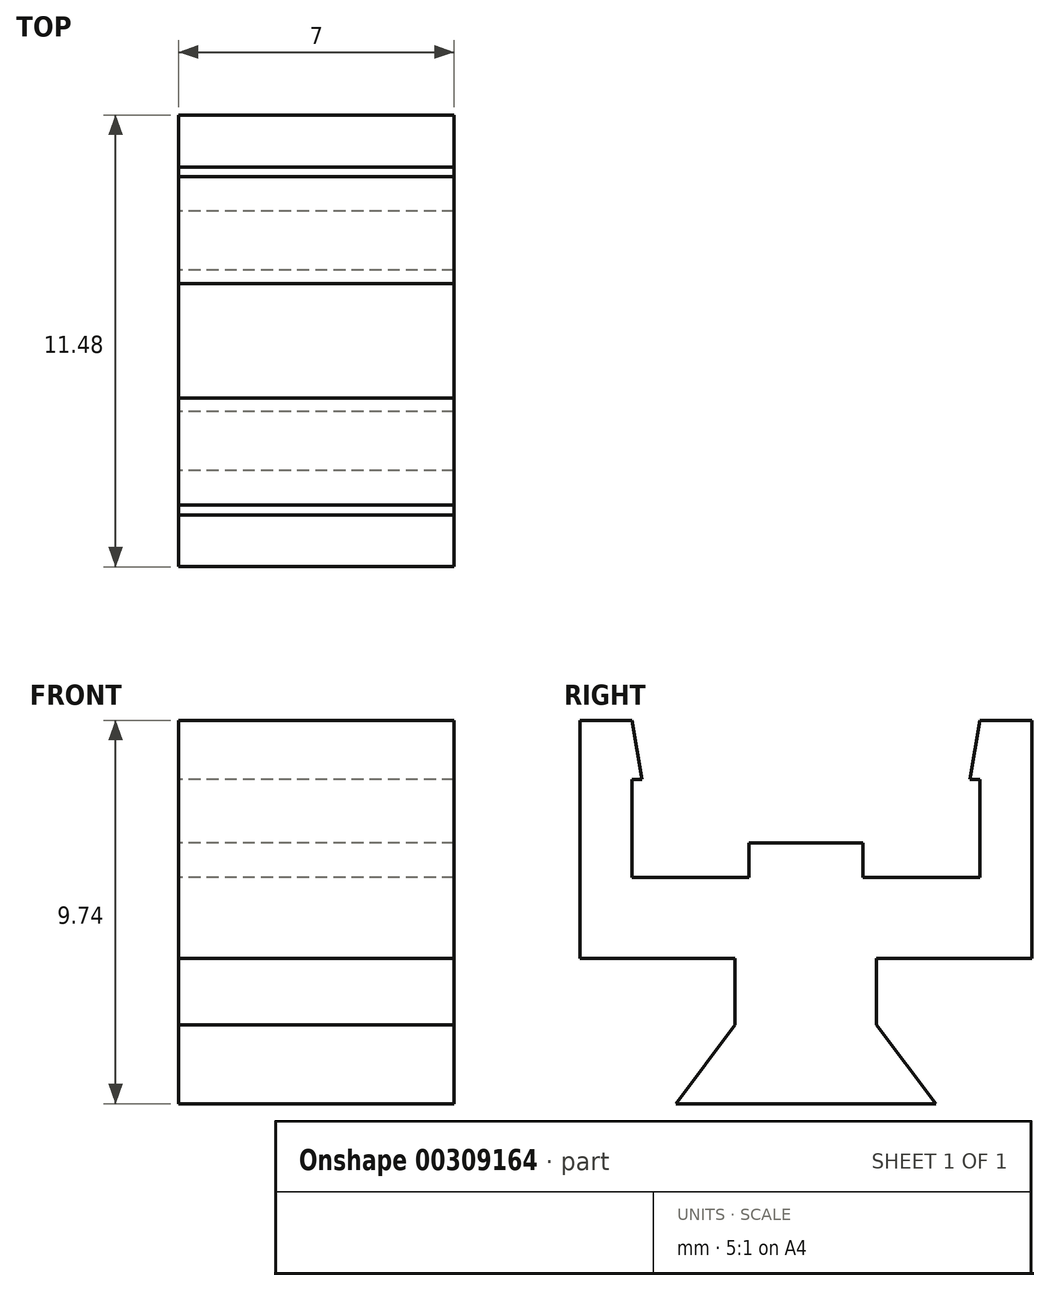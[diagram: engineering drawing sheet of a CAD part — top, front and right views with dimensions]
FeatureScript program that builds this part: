
annotation { "Feature Type Name" : "Feature", "Feature Type Description" : "" }
export const myFeature = defineFeature(function(context is Context, id is Id, definition is map)
    precondition{}
    {
        {
            var Q0;
            Q0=qCreatedBy(makeId("Right.planeOp"),FACE);
            var sketch = newSketch(context, id + "F0", { "sketchPlane" : qUnion([Q0])});
            skLineSegment(sketch, "E0", {"start": v(-2.14, -4.23) * mm, "end": v(1.46, -4.23) * mm, "construction": true});
            skLineSegment(sketch, "E1", {"start": v(-2.14, -4.23) * mm, "end": v(-3.34, -4.23) * mm, "construction": true});
            skLineSegment(sketch, "E2", {"start": v(1.46, -4.23) * mm, "end": v(2.66, -4.23) * mm, "construction": true});
            skLineSegment(sketch, "E3", {"start": v(-2.14, -4.23) * mm, "end": v(-2.14, -2.54) * mm});
            skLineSegment(sketch, "E4.MirrorCS", {"start": v(1.46, -4.23) * mm, "end": v(1.46, -2.54) * mm});
            skLineSegment(sketch, "E5", {"start": v(-2.14, -2.54) * mm, "end": v(1.46, -2.54) * mm});
            skLineSegment(sketch, "E6", {"start": v(-2.14, -4.23) * mm, "end": v(1.46, -4.23) * mm});
            skLineSegment(sketch, "E7.bottom", {"start": v(1.46, -2.54) * mm, "end": v(2.66, -2.54) * mm});
            skLineSegment(sketch, "E8.MirrorCS", {"start": v(-2.14, -2.54) * mm, "end": v(-3.34, -2.54) * mm});
            skLineSegment(sketch, "E9", {"start": v(-3.34, -2.54) * mm, "end": v(-3.34, -0.49) * mm});
            skLineSegment(sketch, "E10", {"start": v(-3.34, -0.49) * mm, "end": v(-0.34, -0.49) * mm});
            skLineSegment(sketch, "E11.MirrorCS", {"start": v(2.66, -0.49) * mm, "end": v(-0.34, -0.49) * mm});
            skLineSegment(sketch, "E12.MirrorCS", {"start": v(2.66, -2.54) * mm, "end": v(2.66, -0.49) * mm});
            skLineSegment(sketch, "E13", {"start": v(-1.8, -0.49) * mm, "end": v(-1.8, 0.4) * mm});
            skLineSegment(sketch, "E14", {"start": v(-1.8, 0.4) * mm, "end": v(-0.34, 0.4) * mm});
            skLineSegment(sketch, "E15.MirrorCS", {"start": v(1.1, 0.4) * mm, "end": v(-0.34, 0.4) * mm});
            skLineSegment(sketch, "E16.MirrorCS", {"start": v(1.1, -0.49) * mm, "end": v(1.1, 0.4) * mm});
            skLineSegment(sketch, "E17", {"start": v(4.08, -0.49) * mm, "end": v(4.08, 2.01) * mm});
            skLineSegment(sketch, "E18.MirrorCS", {"start": v(-4.76, -0.49) * mm, "end": v(-4.76, 2.01) * mm});
            skLineSegment(sketch, "E19", {"start": v(-4.76, 2.01) * mm, "end": v(-4.5, 2.01) * mm});
            skLineSegment(sketch, "E20", {"start": v(-4.76, 3.51) * mm, "end": v(-6.08, 3.51) * mm});
            skLineSegment(sketch, "E21", {"start": v(-6.08, 3.51) * mm, "end": v(-6.08, -2.54) * mm});
            skLineSegment(sketch, "E22", {"start": v(-6.08, -2.54) * mm, "end": v(-3.34, -2.54) * mm});
            skLineSegment(sketch, "E23.MirrorCS", {"start": v(4.08, 3.51) * mm, "end": v(5.4, 3.51) * mm});
            skLineSegment(sketch, "E24.MirrorCS", {"start": v(5.4, 3.51) * mm, "end": v(5.4, -2.54) * mm});
            skLineSegment(sketch, "E25.MirrorCS", {"start": v(5.4, -2.54) * mm, "end": v(2.66, -2.54) * mm});
            skLineSegment(sketch, "E26.MirrorCS", {"start": v(4.08, 2.01) * mm, "end": v(3.83, 2.01) * mm});
            skLineSegment(sketch, "E27", {"start": v(-4.76, -0.49) * mm, "end": v(-3.34, -0.49) * mm});
            skLineSegment(sketch, "E28", {"start": v(2.66, -0.49) * mm, "end": v(4.08, -0.49) * mm});
            skPoint(sketch, "E29.end.orphan", {"position": v(-3.75, 3.51) * mm});
            skPoint(sketch, "E30.MirrorCS.end.orphan", {"position": v(3.07, 3.51) * mm});
            skPoint(sketch, "E30.MirrorCS.start.orphan", {"position": v(3.07, 2.01) * mm});
            skPoint(sketch, "E31.end.orphan", {"position": v(-4.26, 3.51) * mm});
            skLineSegment(sketch, "E32", {"start": v(-4.76, 3.51) * mm, "end": v(-4.5, 2.01) * mm});
            skPoint(sketch, "E33.orphan", {"position": v(-4.26, 2.01) * mm});
            skLineSegment(sketch, "E34.MirrorCS", {"start": v(4.08, 3.51) * mm, "end": v(3.83, 2.01) * mm});
            skPoint(sketch, "E35.MirrorCS.end.orphan", {"position": v(3.58, 3.51) * mm});
            skPoint(sketch, "E36.MirrorCS.start.orphan", {"position": v(3.58, 2.01) * mm});
            skLineSegment(sketch, "E37", {"start": v(-2.14, -4.23) * mm, "end": v(-2.14, -6.23) * mm});
            skLineSegment(sketch, "E38", {"start": v(1.46, -4.23) * mm, "end": v(1.46, -6.23) * mm});
            skLineSegment(sketch, "E39", {"start": v(1.46, -6.23) * mm, "end": v(-2.14, -6.23) * mm});
            skLineSegment(sketch, "E40", {"start": v(1.46, -6.23) * mm, "end": v(2.96, -6.23) * mm});
            skLineSegment(sketch, "E41", {"start": v(1.46, -4.23) * mm, "end": v(2.96, -6.23) * mm});
            skLineSegment(sketch, "E42", {"start": v(-2.14, -6.23) * mm, "end": v(-3.64, -6.23) * mm});
            skLineSegment(sketch, "E43", {"start": v(-3.64, -6.23) * mm, "end": v(-2.14, -4.23) * mm});
            skSolve(sketch);
        }
        {
            var Q0;
            Q0 = qSketchRegion(id + "F0", true);
            extrude(context, id + "F1", {"entities" : qUnion([Q0]), "depth" : 7 * mm});
        }
    });
